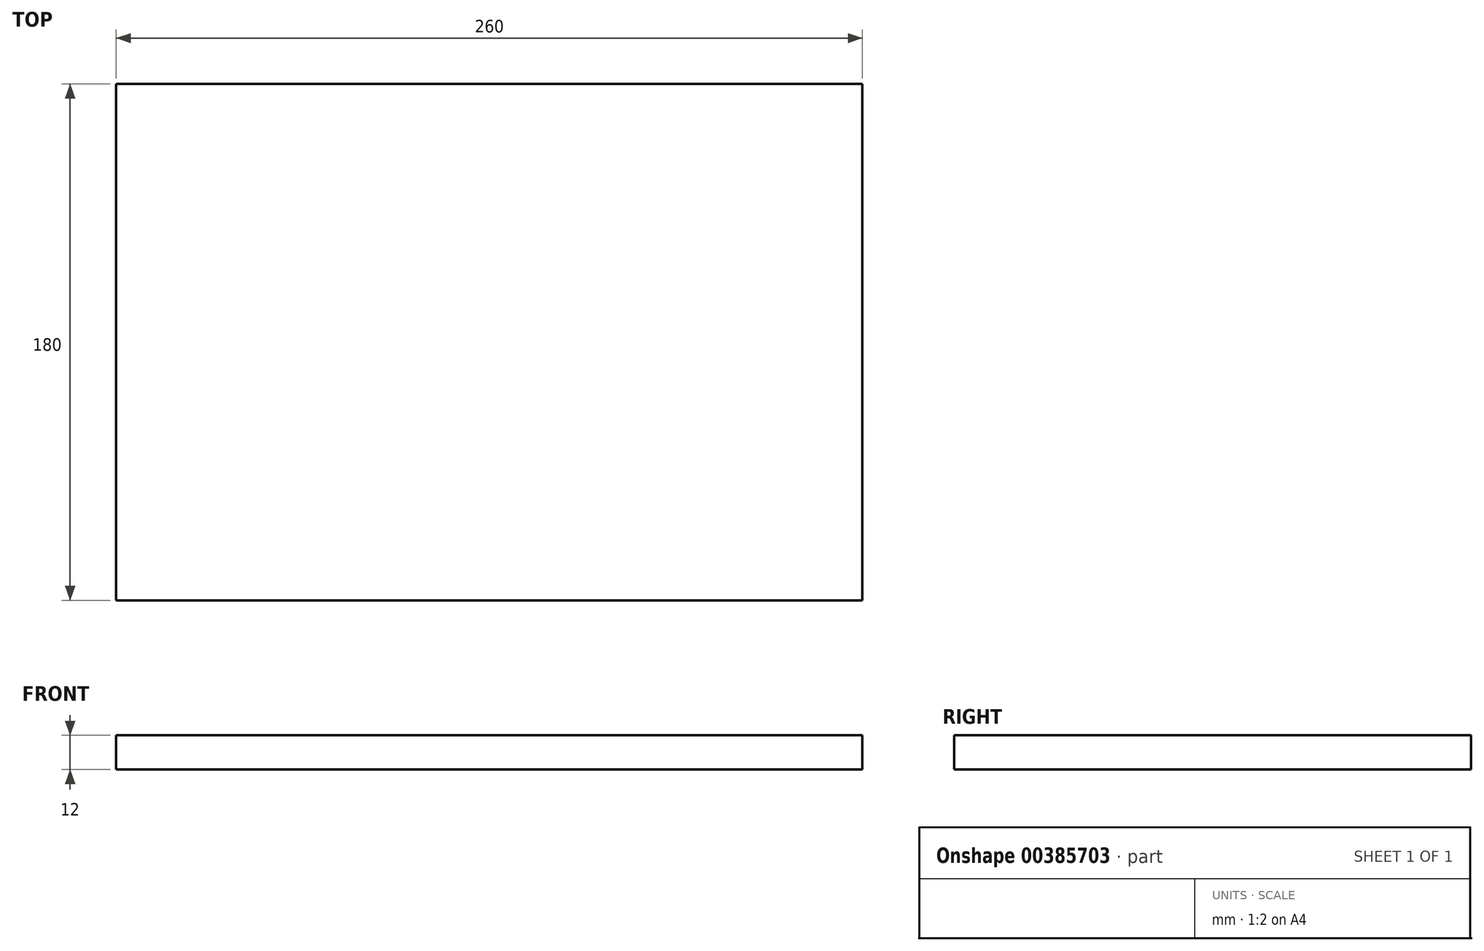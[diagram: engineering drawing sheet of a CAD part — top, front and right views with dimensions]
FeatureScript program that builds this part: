
annotation { "Feature Type Name" : "Feature", "Feature Type Description" : "" }
export const myFeature = defineFeature(function(context is Context, id is Id, definition is map)
    precondition{}
    {
        {
            var Q0;
            Q0=qCreatedBy(makeId("Top.planeOp"),FACE);
            var sketch = newSketch(context, id + "F0", { "sketchPlane" : qUnion([Q0])});
            skLineSegment(sketch, "E0.bottom", {"start": v(130, -90) * mm, "end": v(-130, -90) * mm});
            skLineSegment(sketch, "E0.top", {"start": v(130, 90) * mm, "end": v(-130, 90) * mm});
            skLineSegment(sketch, "E0.left", {"start": v(130, -90) * mm, "end": v(130, 90) * mm});
            skLineSegment(sketch, "E0.right", {"start": v(-130, -90) * mm, "end": v(-130, 90) * mm});
            skPoint(sketch, "E0.middle", {"position": v(0, 0) * mm});
            skSolve(sketch);
        }
        {
            var Q0;
            Q0=makeQuery(id+"F0.imprint","IMPRINT",FACE,{"disambiguationData":[TD([[makeQuery(id+"F0.imprint","IMPRINT",EDGE,{"derivedFrom":sQuery(id+"F0.wireOp",EDGE,"E0.bottom")}),-1.0]])]});
            extrude(context, id + "F1", {"entities" : qUnion([Q0]), "depth" : 12 * mm});
        }
    });
